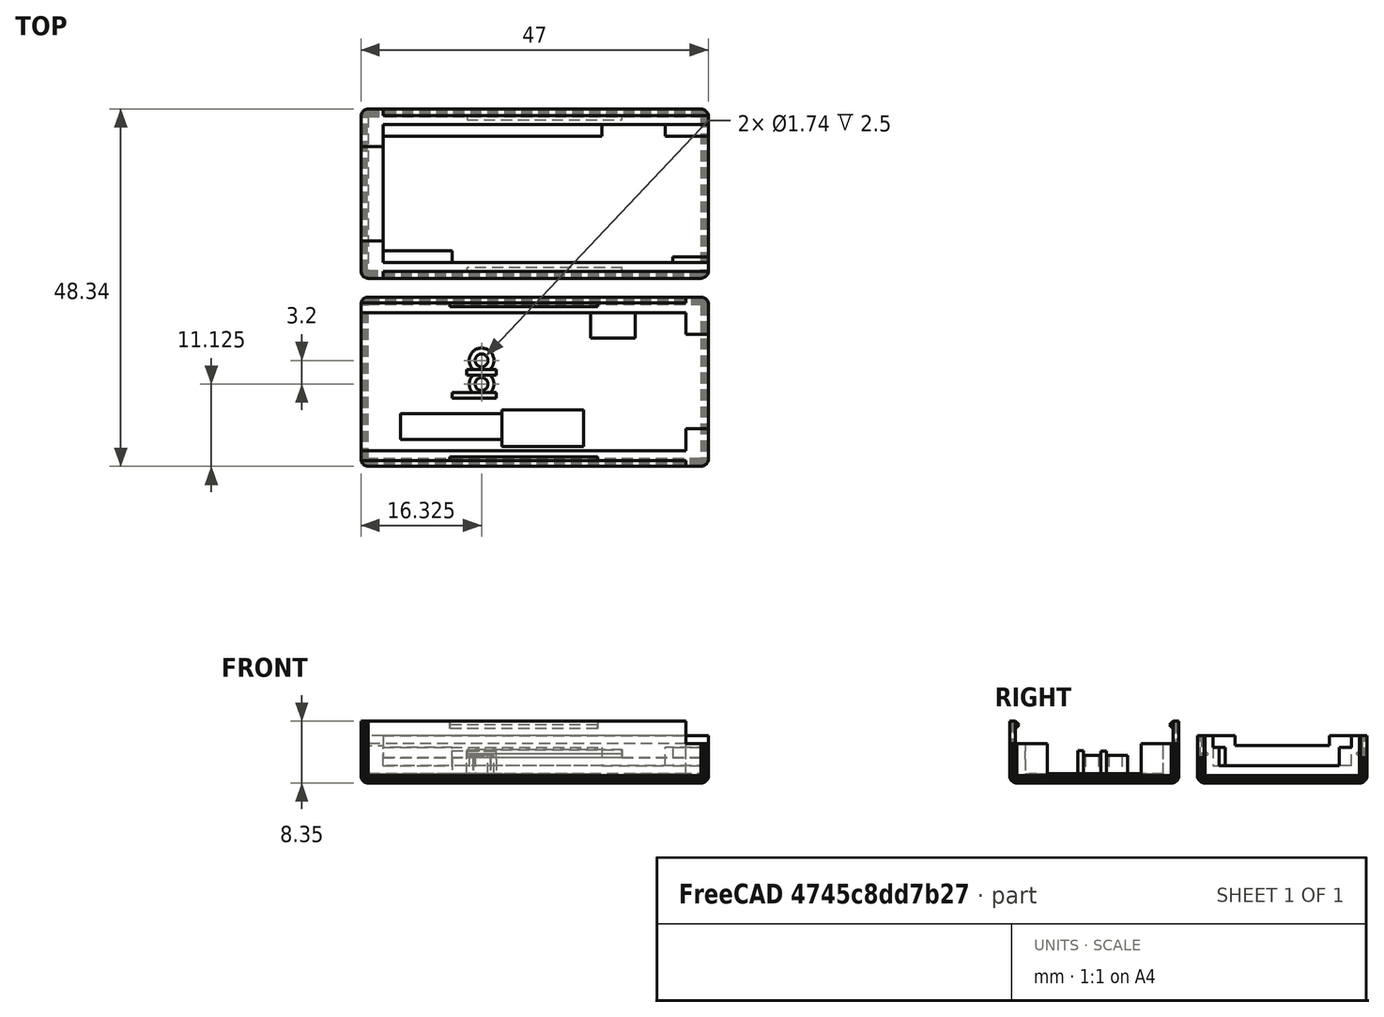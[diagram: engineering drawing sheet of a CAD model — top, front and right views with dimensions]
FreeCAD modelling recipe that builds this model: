
FCSTD DOCUMENT  (FreeCAD 0.14R3703 (Git))
Label: usb_asp
License: CC-BY 3.0
LicenseURL: http://creativecommons.org/licenses/by/3.0/
objects: Part::Extrusion×9, Part::Part2DObjectPython×6, Part::Cut×5, Part::Feature×4, Part::MultiFuse×2, Part::Thickness×2, App::MeasureDistance×1
note: 28 computed .brp shape members not serialized (recipe doc carries the construction recipe); baked Part::Feature solids carry a one-line shape summary decoded from their .brp

FEATURE [Part::Feature] Solid_rev  label="top (Rev)"
  shape: bbox 47 x 22.9 x 7.85 mm, 789 faces (baked)
FEATURE [Part::Feature] Solid001_rev  label="bottom (Rev)"
  shape: bbox 47 x 22.9 x 6.4 mm, 720 faces (baked)
FEATURE [Part::Feature] Solid_rev001  label="top (Rev)001"
  shape: bbox 47 x 22.9 x 7.85 mm, 789 faces (baked)
FEATURE [Part::Extrusion] Extrude
  Dir = (0,0,5)
  Solid = true
FEATURE [Part::Cut] Cut
  Base = -> Solid_rev
  Tool = -> Extrude
FEATURE [Part::Cut] Cut001
  Base = -> Solid_rev001
  Placement = pos=(0,0,0.5) rot=(0,0,1;0rad)
FEATURE [Part::Feature] Cut_cs
  shape: bbox 47 x 22.9 x 2e-07 mm, 0 faces, 0 solids (baked)
FEATURE [Part::Extrusion] Extrude002
  Base = -> Cut_cs
  Dir = (0,0,1.1)
  Solid = true
FEATURE [Part::Part2DObjectPython] Rectangle001  # Draft 2D object (typed FeaturePython)
  ChamferSize = 0
  FilletRadius = 0
  Height = -3.45
  Length = 13.75
  MakeFace = false
  Placement = pos=(-18.15,-17.07,3.25) rot=(0,0,1;0rad)
  Support = -> Cut
FEATURE [Part::Part2DObjectPython] Rectangle002  # Draft 2D object (typed FeaturePython)
  ChamferSize = 0
  FilletRadius = 0
  Height = -3.45
  Length = 6
  MakeFace = false
  Placement = pos=(7.6,-3.37,3.25) rot=(0,0,1;0rad)
  Support = -> Cut
FEATURE [Part::Part2DObjectPython] Rectangle003  # Draft 2D object (typed FeaturePython)
  ChamferSize = 0
  FilletRadius = 0
  Height = -0.75
  Length = 6
  MakeFace = false
  Placement = pos=(-11.175,-14.2072,3.25) rot=(0,0,1;0rad)
  Support = -> Cut
FEATURE [Part::Extrusion] Extrude003
  Base = -> Rectangle001
  Dir = (0,0,-5)
  Solid = true
FEATURE [Part::Cut] Cut002
  Base = -> Cut
  Tool = -> Extrude003
FEATURE [Part::Extrusion] Extrude004
  Base = -> Rectangle002
  Dir = (0,0,-5)
  Solid = true
FEATURE [Part::Cut] Cut003
  Base = -> Cut002
  Tool = -> Extrude004
FEATURE [Part::Extrusion] Extrude005
  Base = -> Rectangle003
  Dir = (0,0,-2)
  Solid = true
FEATURE [Part::Extrusion] Extrude006
  Base = -> Rectangle003
  Dir = (0,0,1.1)
  Solid = true
FEATURE [Part::MultiFuse] Fusion
  Shapes = -> [Extrude006,Cut001,Extrude002,Extrude005,Cut003]
FEATURE [Part::Part2DObjectPython] Rectangle  # Draft 2D object (typed FeaturePython)
  ChamferSize = 0
  FilletRadius = 0
  Height = 5
  Length = 11
  MakeFace = false
  Placement = pos=(-4.4,-21.5158,1.25) rot=(0,0,1;0rad)
  Support = -> Fusion
FEATURE [Part::Extrusion] Extrude007
  Base = -> Rectangle
  Dir = (0,0,-0.25)
  Solid = true
FEATURE [Part::Cut] Cut004
  Base = -> Fusion
  Tool = -> Extrude007
FEATURE [Part::Part2DObjectPython] Circle  # Draft 2D object (typed FeaturePython)
  FirstAngle = 0
  LastAngle = 0
  MakeFace = false
  Placement = pos=(-7.175,-9.84501,1.25) rot=(0,0,1;0rad)
  Radius = 0.871654
FEATURE [Part::Part2DObjectPython] Circle001  # Draft 2D object (typed FeaturePython)
  FirstAngle = 0
  LastAngle = 0
  MakeFace = false
  Placement = pos=(-7.175,-13.045,1.25) rot=(0,0,1;0rad)
  Radius = 0.871654
FEATURE [Part::Extrusion] Extrude008
  Base = -> Circle
  Dir = (0,0,2.5)
  Solid = true
FEATURE [Part::Extrusion] Extrude009
  Base = -> Circle001
  Dir = (0,0,2.5)
  Solid = true
FEATURE [Part::Thickness] Thickness
  Faces = -> Extrude008 [Face3,Face2]
  Intersection = false
  Join = 0
  Mode = 0
  SelfIntersection = false
  Value = 0.8
FEATURE [Part::Thickness] Thickness001
  Faces = -> Extrude009 [Face3,Face2]
  Intersection = false
  Join = 0
  Mode = 0
  SelfIntersection = false
  Value = 0.8
FEATURE [Part::MultiFuse] Fusion001
  Shapes = -> [Thickness001,Thickness,Cut004]
FEATURE [App::MeasureDistance] Distance  label="Distance: 29.103"
  Distance = 1.1
  P1 = (0,0,4.25)
  P2 = (0,0,5.35)
